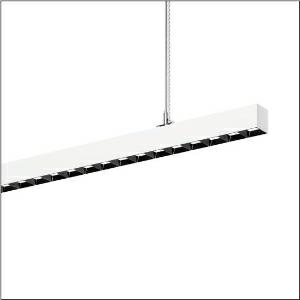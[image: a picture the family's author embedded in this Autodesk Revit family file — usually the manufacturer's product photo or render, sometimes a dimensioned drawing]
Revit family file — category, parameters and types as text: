
# Revit family: silica_r__21_51mx31tctdw_2edc
name_source: partatom
category: Lighting Fixtures
units: mm (PartAtom-declared; Revit-internal decimal feet)

## family parameters
Cut with Voids When Loaded = No
Host = Face
Light Source = No
Part Type = Normal
Room Calculation Point = No
Round Connector Dimension = Use Diameter
Shared = No

## types (1)
- --- (1 x LED, 15550 lm, 133.9 W, 6500K)
    Apparent Load = 134 VA
    CIE Flux Codes = 85 99 100 60 100
    Color Rendering = 80
    Color Temperature = 6500K
    Default Elevation = 1800 mm
    Description = Silica® 21, office luminaire, primary light control with darklight reflector, of PMMA, black, CAT 2 (L<= 3000cd/m²), light emission: direct/indirect distribution, primary light characteristic: symmetric, installation type: suspended mounting, LED, rated luminous flux: 15.550lm, luminous efficacy: 111lm/W, light colour: 8tw, colour temperature: 2700..6500K, control gear: DALI DT8, with terminal, 3+2-pole, max. 2.5mm², mains connection: 220..240V, AC, 50/60Hz, rated input power: 140.6W, luminaire housing, of aluminium, traffic white (RAL 9016), length: 3.004mm, width: 53mm, height: 53mm, protection rating (complete): IP20, insulation class (complete): insulation class I (protective earthing), certification: CE, permissible operating ambient temperature: 0..+35°C, standard: EN 50419, packaging unit: 1 piece
    Height = 53 mm
    Lamp = 1 x LED
    Lamp Light Flux = 15550 lm
    Lamp Power = 133.9 W
    Lamp count = 1
    Length = 3004 mm
    Luminous efficacy = 116 lm/W
    Manufacturer = Siteco
    ModVariant = No
    Model = 51MX31TCTDW
    Mounting Place = Ceiling
    Mounting Type = Pendant
    Number of Poles = 1
    OnlyDefault = Yes
    Power Factor = 1
    Product Name = Silica® 21
    Product group = office luminaire | ceiling pendant
    ProductGroupID = 904
    Protection Class = Protection class I
    Protection Degree = IP 20
    RLX_Detail_Level = 1
    RLX_Emergency_Light_Flux = 0 lm
    RLX_Emergency_Type = 0
    RLX_Emergency_Type_DB = No
    RlxData = <blob elided: 61297 chars, md5=fb367137>
    Socket = socket
    Standby Power = 0 W
    System Light Flux = 15550 lm
    System Power = 134 W
    Type Comments = individual setting
    Type Image = l_1335871.jpg
    URL = http://relux.com
    VarID = @adj_139896
    Voltage = 0 V
    Weight = 0.00 kg
    Width = 53 mm

## geometry (parser evidence)
native form markers: Blend x4, Sweep x13
no freeform markers — native parametric forms only
